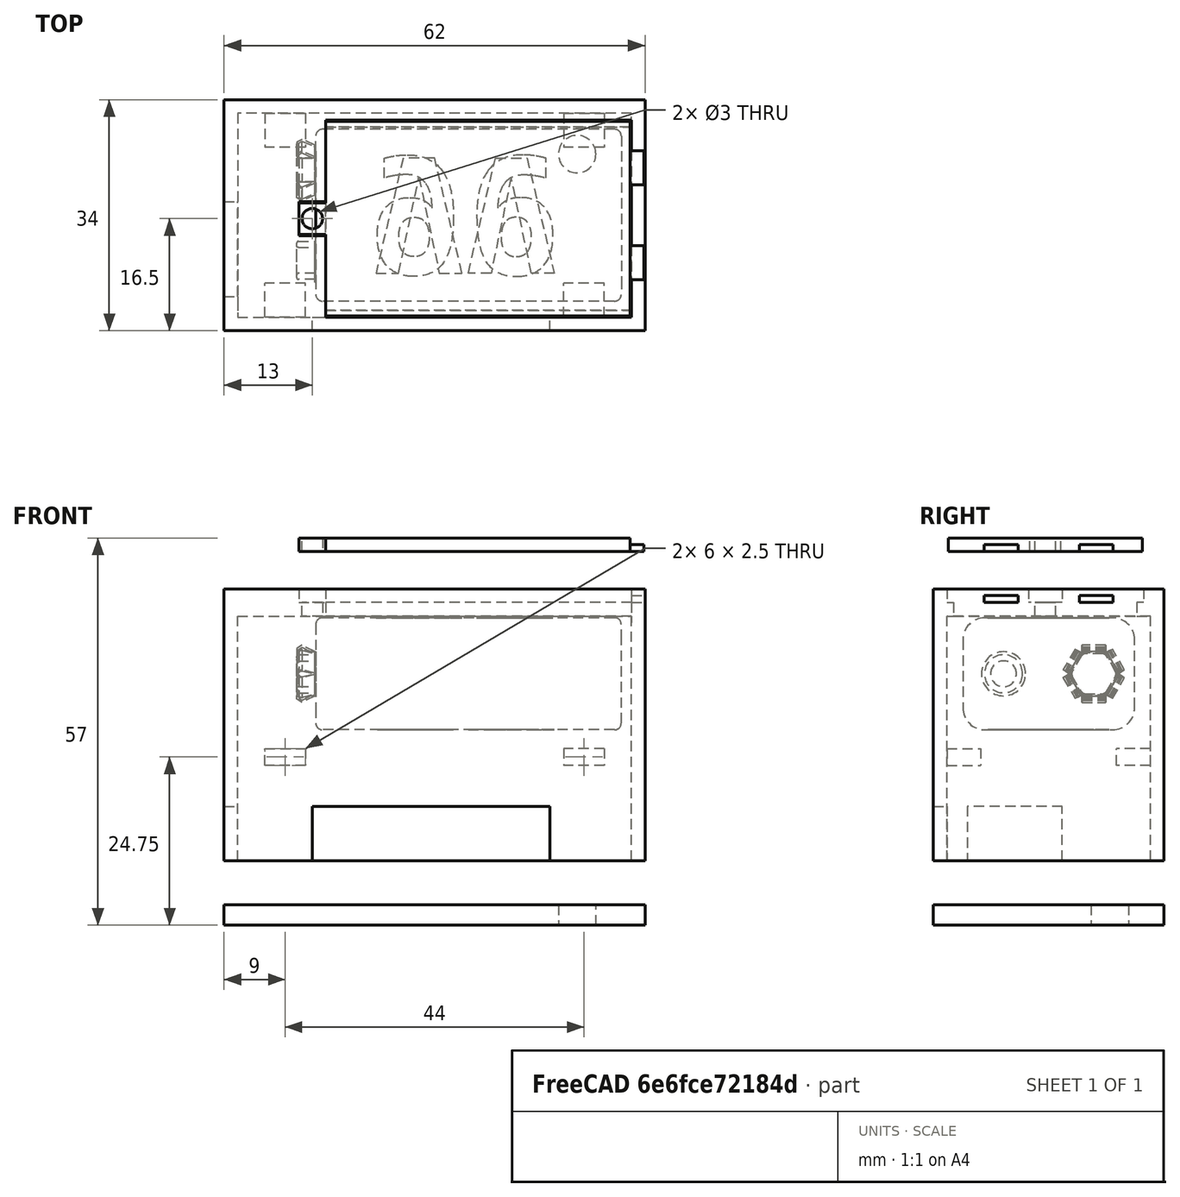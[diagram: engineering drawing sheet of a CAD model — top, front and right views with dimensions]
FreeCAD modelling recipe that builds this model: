
FCSTD DOCUMENT  (FreeCAD 0.20R29603 (Git))
Label: Remote Housing Revision 2
License: All rights reserved
LicenseURL: http://en.wikipedia.org/wiki/All_rights_reserved
objects: Sketcher::SketchObject×15, PartDesign::Pocket×9, PartDesign::Pad×6, Mesh::Feature×4, PartDesign::Body×3, Part::Feature×1
note: 49 computed .brp shape members not serialized (recipe doc carries the construction recipe); baked Part::Feature solids carry a one-line shape summary decoded from their .brp

FEATURE [Mesh::Feature] Unnamed_Goouuu_ESP32_Development_Board001  label="ESP32_Development_Board"
  Placement = pos=(-3.3e-15,12,-7) rot=(-0.57735,-0.57735,0.57735;2.0944rad)
FEATURE [Mesh::Feature] Switch
  Placement = pos=(-21,16,-13) rot=(0,0,1;1.5708rad)
FEATURE [Mesh::Feature] Switch001
  Placement = pos=(19,5,-19.5) rot=(-1,0,0;3.14159rad)
FEATURE [Mesh::Feature] Switch002
  Placement = pos=(-1.5,5,-19.5) rot=(1,0,0;3.14159rad)
FEATURE [Part::Feature] Solid  label="9V Battery"
  Placement = pos=(27.5,12,7) rot=(0.57735,-0.57735,-0.57735;2.0944rad)
  shape: bbox 47.8 x 25.84 x 17.04 mm, 172 faces (baked)
FEATURE [Sketcher::SketchObject] Sketch
  AttachmentOffset = pos=(0,0,16) rot=(0,0,1;0rad)
  FullyConstrained = true
  MapMode = 5
  Placement = pos=(0,0,16) rot=(0,0,1;0rad)
  Support = -> [XY_Plane]
  sketch-geometry (4):
    g0: LineSegment StartX=-31 StartY=29 StartZ=0 EndX=31 EndY=29 EndZ=0
    g1: LineSegment StartX=31 StartY=29 StartZ=0 EndX=31 EndY=-5 EndZ=0
    g2: LineSegment StartX=31 StartY=-5 StartZ=0 EndX=-31 EndY=-5 EndZ=0
    g3: LineSegment StartX=-31 StartY=-5 StartZ=0 EndX=-31 EndY=29 EndZ=0
  constraints (12):
    c: Horizontal(g0)
    c: Vertical(g1)
    c: Horizontal(g2)
    c: Vertical(g3)
    c: Coincident(g0,g3)
    c: Coincident(g2,g3)
    c: Coincident(g2,g1)
    c: Coincident(g1,g0)
    c: DistanceX(g-1,g1) = 31
    c: DistanceX(g2,g-1) = 31
    c: DistanceY(g-1,g0) = 29
    c: DistanceY(g1,g-1) = 5
FEATURE [PartDesign::Pad] Pad
  Direction = (0,0,1)
  Length = 40
  Length2 = 10
  Profile = -> Sketch
  ReferenceAxis = -> Sketch [N_Axis]
  Type = 0
FEATURE [Sketcher::SketchObject] Sketch001  label="Internal Cutout"
  FullyConstrained = true
  MapMode = 5
  Placement = pos=(0,0,16) rot=(1,0,0;3.14159rad)
  Support = -> [Pad]
  sketch-geometry (4):
    g0: LineSegment StartX=-29 StartY=-27 StartZ=0 EndX=-29 EndY=3 EndZ=0
    g1: LineSegment StartX=-29 StartY=3 StartZ=0 EndX=29 EndY=3 EndZ=0
    g2: LineSegment StartX=29 StartY=3 StartZ=0 EndX=29 EndY=-27 EndZ=0
    g3: LineSegment StartX=29 StartY=-27 StartZ=0 EndX=-29 EndY=-27 EndZ=0
  constraints (12):
    c: Vertical(g0)
    c: Horizontal(g1)
    c: Vertical(g2)
    c: Horizontal(g3)
    c: Coincident(g0,g1)
    c: Coincident(g0,g3)
    c: Coincident(g2,g3)
    c: Coincident(g1,g2)
    c: DistanceX(g-1,g1) = 29
    c: DistanceX(g0,g-1) = 29
    c: DistanceY(g2,g-1) = 27
    c: DistanceY(g-1,g1) = 3
FEATURE [PartDesign::Pocket] Pocket
  BaseFeature = -> Pad
  Direction = (0,0,1)
  Length = 36
  Length2 = 5
  Profile = -> Sketch001
  ReferenceAxis = -> Sketch001 [N_Axis]
  Type = 0
FEATURE [Sketcher::SketchObject] Sketch002  label="Battery Door Hole"
  FullyConstrained = true
  MapMode = 5
  Placement = pos=(0,0,56) rot=(0,0,1;0rad)
  Support = -> [Pocket]
  sketch-geometry (4):
    g0: LineSegment StartX=-16 StartY=25 StartZ=0 EndX=29 EndY=25 EndZ=0
    g1: LineSegment StartX=29 StartY=25 StartZ=0 EndX=29 EndY=-2 EndZ=0
    g2: LineSegment StartX=29 StartY=-2 StartZ=0 EndX=-16 EndY=-2 EndZ=0
    g3: LineSegment StartX=-16 StartY=-2 StartZ=0 EndX=-16 EndY=25 EndZ=0
  constraints (12):
    c: Horizontal(g0)
    c: Vertical(g1)
    c: Horizontal(g2)
    c: Vertical(g3)
    c: Coincident(g3,g0)
    c: Coincident(g1,g0)
    c: Coincident(g1,g2)
    c: Coincident(g2,g3)
    c: DistanceX(g-1,g1) = 29
    c: DistanceX(g2,g-1) = 16
    c: DistanceY(g-1,g0) = 25
    c: DistanceY(g2,g-1) = 2
FEATURE [PartDesign::Pocket] Pocket001
  BaseFeature = -> Pocket
  Direction = (0,0,-1)
  Length = 5
  Length2 = 5
  Profile = -> Sketch002
  ReferenceAxis = -> Sketch002 [N_Axis]
  Type = 0
FEATURE [Sketcher::SketchObject] Sketch003  label="Battery Door Hole 2"
  FullyConstrained = true
  MapMode = 5
  Placement = pos=(0,0,56) rot=(0,0,1;0rad)
  Support = -> [Pocket001]
  sketch-geometry (8):
    g0: LineSegment StartX=-16 StartY=26 StartZ=0 EndX=29 EndY=26 EndZ=0
    g1: LineSegment StartX=29 StartY=26 StartZ=0 EndX=29 EndY=-3 EndZ=0
    g2: LineSegment StartX=29 StartY=-3 StartZ=0 EndX=-16 EndY=-3 EndZ=0
    g3: LineSegment StartX=-16 StartY=-3 StartZ=0 EndX=-16 EndY=9 EndZ=0
    g4: LineSegment StartX=-20 StartY=9 StartZ=0 EndX=-16 EndY=9 EndZ=0
    g5: LineSegment StartX=-20 StartY=14 StartZ=0 EndX=-16 EndY=14 EndZ=0
    g6: LineSegment StartX=-16 StartY=14 StartZ=0 EndX=-16 EndY=26 EndZ=0
    g7: LineSegment StartX=-20 StartY=14 StartZ=0 EndX=-20 EndY=9 EndZ=0
  constraints (24):
    c: Horizontal(g0)
    c: Vertical(g1)
    c: Horizontal(g2)
    c: Vertical(g3)
    c: Vertical(g6)
    c: Coincident(g0,g6)
    c: Coincident(g6,g5)
    c: Coincident(g4,g3)
    c: Coincident(g3,g2)
    c: Coincident(g2,g1)
    c: Coincident(g0,g1)
    c: DistanceX(g-1,g1) = 29
    c: DistanceX(g2,g-1) = 16
    c: DistanceY(g-1,g0) = 26
    c: DistanceY(g2,g-1) = 3
    c: DistanceY(g-1,g3) = 9
    c: DistanceY(g4,g5) = 5
    c: Vertical(g7)
    c: Coincident(g7,g5)
    c: Coincident(g7,g4)
    c: DistanceX(g4,g-1) = 20
    c: DistanceX(g5,g-1) = 16
    c: DistanceY(g-1,g4) = 9
    c: DistanceY(g-1,g5) = 14
FEATURE [PartDesign::Pocket] Pocket002
  BaseFeature = -> Pocket001
  Direction = (0,0,-1)
  Length = 2
  Length2 = 5
  Profile = -> Sketch003
  ReferenceAxis = -> Sketch003 [N_Axis]
  Type = 0
FEATURE [Sketcher::SketchObject] Sketch004  label="Battery Door Screw Hole"
  FullyConstrained = true
  MapMode = 5
  Placement = pos=(0,0,54) rot=(0,0,1;0rad)
  Support = -> [Pocket002]
  sketch-geometry (1):
    g0: Circle CenterX=-18 CenterY=11.5 CenterZ=0 NormalX=0 NormalY=0 NormalZ=1 AngleXU=0 Radius=1.5
  constraints (3):
    c: Diameter(g0) = 3
    c: DistanceX(g0,g-1) = 18
    c: DistanceY(g-1,g0) = 11.5
FEATURE [PartDesign::Pocket] Pocket003
  BaseFeature = -> Pocket002
  Direction = (0,0,-1)
  Length = 5
  Length2 = 5
  Profile = -> Sketch004
  ReferenceAxis = -> Sketch004 [N_Axis]
  Type = 0
FEATURE [Sketcher::SketchObject] Sketch005  label="Battery Door Hinge"
  FullyConstrained = true
  MapMode = 5
  Placement = pos=(29,0,0) rot=(0.57735,-0.57735,-0.57735;2.0944rad)
  Support = -> [Pocket003]
  sketch-geometry (8):
    g0: LineSegment StartX=-21.5 StartY=55 StartZ=0 EndX=-16.5 EndY=55 EndZ=0
    g1: LineSegment StartX=-16.5 StartY=55 StartZ=0 EndX=-16.5 EndY=54 EndZ=0
    g2: LineSegment StartX=-21.5 StartY=54 StartZ=0 EndX=-16.5 EndY=54 EndZ=0
    g3: LineSegment StartX=-21.5 StartY=55 StartZ=0 EndX=-21.5 EndY=54 EndZ=0
    g4: LineSegment StartX=-7.5 StartY=55 StartZ=0 EndX=-2.5 EndY=55 EndZ=0
    g5: LineSegment StartX=-2.5 StartY=55 StartZ=0 EndX=-2.5 EndY=54 EndZ=0
    g6: LineSegment StartX=-2.5 StartY=54 StartZ=0 EndX=-7.5 EndY=54 EndZ=0
    g7: LineSegment StartX=-7.5 StartY=54 StartZ=0 EndX=-7.5 EndY=55 EndZ=0
  constraints (24):
    c: Horizontal(g0)
    c: Horizontal(g2)
    c: Horizontal(g4)
    c: Horizontal(g6)
    c: Coincident(g4,g7)
    c: Coincident(g7,g6)
    c: Coincident(g6,g5)
    c: Coincident(g5,g4)
    c: Coincident(g0,g1)
    c: Coincident(g1,g2)
    c: Coincident(g3,g2)
    c: Coincident(g0,g3)
    c: DistanceY(g-1,g4) = 55
    c: DistanceX(g4,g-1) = 2.5
    c: DistanceX(g4,g4) = 5
    c: DistanceY(g7,g7) = 1
    c: Angle(g7,g4) = 1.5708
    c: Angle(g5,g6) = 1.5708
    c: DistanceY(g-1,g0) = 55
    c: DistanceX(g0,g4) = 14
    c: DistanceX(g0,g0) = 5
    c: DistanceY(g1,g1) = 1
    c: Angle(g0,g1) = 1.5708
    c: Angle(g2,g3) = 1.5708
FEATURE [PartDesign::Pocket] Pocket004
  BaseFeature = -> Pocket003
  Direction = (1,0,0)
  Length = 5
  Length2 = 5
  Profile = -> Sketch005
  ReferenceAxis = -> Sketch005 [N_Axis]
  Type = 0
FEATURE [Sketcher::SketchObject] Sketch006  label="ESP32 Support 1"
  FullyConstrained = true
  MapMode = 5
  Placement = pos=(0,27,0) rot=(1,0,0;1.5708rad)
  Support = -> [Pocket004]
  sketch-geometry (8):
    g0: LineSegment StartX=-25 StartY=32.5 StartZ=0 EndX=-19 EndY=32.5 EndZ=0
    g1: LineSegment StartX=-19 StartY=32.5 StartZ=0 EndX=-19 EndY=30 EndZ=0
    g2: LineSegment StartX=-19 StartY=30 StartZ=0 EndX=-25 EndY=30 EndZ=0
    g3: LineSegment StartX=-25 StartY=32.5 StartZ=0 EndX=-25 EndY=30 EndZ=0
    g4: LineSegment StartX=19 StartY=32.5 StartZ=0 EndX=25 EndY=32.5 EndZ=0
    g5: LineSegment StartX=25 StartY=32.5 StartZ=0 EndX=25 EndY=30 EndZ=0
    g6: LineSegment StartX=25 StartY=30 StartZ=0 EndX=19 EndY=30 EndZ=0
    g7: LineSegment StartX=19 StartY=30 StartZ=0 EndX=19 EndY=32.5 EndZ=0
  constraints (24):
    c: Horizontal(g0)
    c: Vertical(g1)
    c: Horizontal(g2)
    c: Horizontal(g4)
    c: Horizontal(g6)
    c: Vertical(g7)
    c: Coincident(g7,g4)
    c: Coincident(g4,g5)
    c: Coincident(g5,g6)
    c: Coincident(g6,g7)
    c: Coincident(g0,g1)
    c: Coincident(g1,g2)
    c: Coincident(g2,g3)
    c: Coincident(g3,g0)
    c: DistanceY(g-1,g1) = 30
    c: DistanceY(g-1,g6) = 30
    c: DistanceY(g6,g4) = 2.5
    c: DistanceY(g1,g0) = 2.5
    c: DistanceX(g1,g-1) = 19
    c: DistanceX(g-1,g6) = 19
    c: DistanceX(g0,g0) = 6
    c: DistanceX(g4,g4) = 6
    c: Angle(g5,g6) = 1.5708
    c: Angle(g2,g3) = 1.5708
FEATURE [PartDesign::Pad] Pad001
  BaseFeature = -> Pocket004
  Direction = (0,-1,2e-16)
  Length = 5
  Length2 = 10
  Profile = -> Sketch006
  ReferenceAxis = -> Sketch006 [N_Axis]
  Type = 0
FEATURE [Sketcher::SketchObject] Sketch007  label="ESP32 Support 2"
  FullyConstrained = true
  MapMode = 5
  Placement = pos=(0,-3,0) rot=(0,0.707107,0.707107;3.14159rad)
  Support = -> [Pad001]
  sketch-geometry (8):
    g0: LineSegment StartX=-25 StartY=32.5 StartZ=0 EndX=-19 EndY=32.5 EndZ=0
    g1: LineSegment StartX=-25 StartY=30 StartZ=0 EndX=-19 EndY=30 EndZ=0
    g2: LineSegment StartX=-19 StartY=32.5 StartZ=0 EndX=-19 EndY=30 EndZ=0
    g3: LineSegment StartX=-25 StartY=32.5 StartZ=0 EndX=-25 EndY=30 EndZ=0
    g4: LineSegment StartX=19 StartY=30 StartZ=0 EndX=25 EndY=30 EndZ=0
    g5: LineSegment StartX=25 StartY=30 StartZ=0 EndX=25 EndY=32.5 EndZ=0
    g6: LineSegment StartX=25 StartY=32.5 StartZ=0 EndX=19 EndY=32.5 EndZ=0
    g7: LineSegment StartX=19 StartY=32.5 StartZ=0 EndX=19 EndY=30 EndZ=0
  constraints (24):
    c: Horizontal(g0)
    c: Horizontal(g4)
    c: Vertical(g7)
    c: Coincident(g6,g7)
    c: Coincident(g7,g4)
    c: Coincident(g4,g5)
    c: Coincident(g5,g6)
    c: Coincident(g2,g0)
    c: Coincident(g2,g1)
    c: Coincident(g1,g3)
    c: Coincident(g0,g3)
    c: DistanceY(g-1,g4) = 30
    c: DistanceY(g-1,g1) = 30
    c: DistanceY(g4,g6) = 2.5
    c: DistanceY(g2,g2) = 2.5
    c: DistanceX(g-1,g6) = 19
    c: DistanceX(g0,g-1) = 19
    c: DistanceX(g0,g0) = 6
    c: DistanceX(g6,g6) = 6
    c: Angle(g5,g4) = 1.5708
    c: Angle(g7,g6) = 1.5708
    c: Angle(g2,g1) = 1.5708
    c: Angle(g3,g0) = 1.5708
    c: DistanceY(g3,g3) = 2.5
FEATURE [PartDesign::Pad] Pad002
  BaseFeature = -> Pad001
  Direction = (0,1,-2e-16)
  Length = 5
  Length2 = 10
  Profile = -> Sketch007
  ReferenceAxis = -> Sketch007 [N_Axis]
  Type = 0
FEATURE [Sketcher::SketchObject] Sketch008  label="Top Switch Hole"
  FullyConstrained = true
  MapMode = 5
  Placement = pos=(-31,0,0) rot=(0.57735,-0.57735,-0.57735;2.0944rad)
  Support = -> [Pad002]
  sketch-geometry (4):
    g0: LineSegment StartX=-14 StartY=24 StartZ=0 EndX=0 EndY=24 EndZ=0
    g1: LineSegment StartX=0 StartY=24 StartZ=0 EndX=0 EndY=16 EndZ=0
    g2: LineSegment StartX=0 StartY=16 StartZ=0 EndX=-14 EndY=16 EndZ=0
    g3: LineSegment StartX=-14 StartY=16 StartZ=0 EndX=-14 EndY=24 EndZ=0
  constraints (12):
    c: Horizontal(g0)
    c: Vertical(g1)
    c: Horizontal(g2)
    c: Vertical(g3)
    c: Coincident(g0,g3)
    c: Coincident(g2,g3)
    c: Coincident(g1,g2)
    c: Coincident(g1,g0)
    c: DistanceY(g-1,g1) = 16
    c: DistanceX(g1,g-1) = 0
    c: DistanceX(g0,g0) = 14
    c: DistanceY(g1,g1) = 8
FEATURE [PartDesign::Pocket] Pocket005
  BaseFeature = -> Pad002
  Direction = (1,0,0)
  Length = 5
  Length2 = 5
  Profile = -> Sketch008
  ReferenceAxis = -> Sketch008 [N_Axis]
  Type = 0
FEATURE [Sketcher::SketchObject] Sketch009  label="Switch Holes 2"
  FullyConstrained = true
  MapMode = 5
  Placement = pos=(0,-5,0) rot=(1,0,0;1.5708rad)
  Support = -> [Pocket005]
  sketch-geometry (4):
    g0: LineSegment StartX=-18 StartY=16 StartZ=0 EndX=17 EndY=16 EndZ=0
    g1: LineSegment StartX=17 StartY=16 StartZ=0 EndX=17 EndY=24 EndZ=0
    g2: LineSegment StartX=17 StartY=24 StartZ=0 EndX=-18 EndY=24 EndZ=0
    g3: LineSegment StartX=-18 StartY=24 StartZ=0 EndX=-18 EndY=16 EndZ=0
  constraints (12):
    c: Horizontal(g0)
    c: Vertical(g1)
    c: Horizontal(g2)
    c: Vertical(g3)
    c: Coincident(g2,g3)
    c: Coincident(g2,g1)
    c: Coincident(g1,g0)
    c: Coincident(g3,g0)
    c: DistanceX(g-1,g0) = 17
    c: DistanceY(g-1,g0) = 16
    c: DistanceX(g0,g0) = 35
    c: DistanceY(g1,g1) = 8
FEATURE [PartDesign::Pocket] Pocket006
  BaseFeature = -> Pocket005
  Direction = (0,1,-2e-16)
  Length = 5
  Length2 = 5
  Profile = -> Sketch009
  ReferenceAxis = -> Sketch009 [N_Axis]
  Type = 0
FEATURE [PartDesign::Body] Body  label="Housing Bottom"
  Group = -> [Sketch,Pad,Sketch001,Pocket,Sketch002,Pocket001,Sketch003,Pocket002,Sketch004,Pocket003,Sketch005,Pocket004,Sketch006,Pad001,Sketch007,Pad002,Sketch008,Pocket005,Sketch009,Pocket006]
  Origin = -> Origin
  Placement = pos=(0,0,-36.5) rot=(0,0,1;0rad)
  Tip = -> Pocket006
FEATURE [Sketcher::SketchObject] Sketch010  label="Battery Cover001"
  AttachmentOffset = pos=(0,0,25) rot=(0,0,1;0rad)
  FullyConstrained = true
  MapMode = 5
  Placement = pos=(0,0,25) rot=(0,0,1;0rad)
  Support = -> [XY_Plane001]
  sketch-geometry (8):
    g0: LineSegment StartX=-16 StartY=25.8 StartZ=0 EndX=28.8 EndY=25.8 EndZ=0
    g1: LineSegment StartX=28.8 StartY=25.8 StartZ=0 EndX=28.8 EndY=-2.8 EndZ=0
    g2: LineSegment StartX=28.8 StartY=-2.8 StartZ=0 EndX=-16 EndY=-2.8 EndZ=0
    g3: LineSegment StartX=-16 StartY=-2.8 StartZ=0 EndX=-16 EndY=9.2 EndZ=0
    g4: LineSegment StartX=-16 StartY=9.2 StartZ=0 EndX=-20 EndY=9.2 EndZ=0
    g5: LineSegment StartX=-20 StartY=9.2 StartZ=0 EndX=-20 EndY=13.8 EndZ=0
    g6: LineSegment StartX=-20 StartY=13.8 StartZ=0 EndX=-16 EndY=13.8 EndZ=0
    g7: LineSegment StartX=-16 StartY=13.8 StartZ=0 EndX=-16 EndY=25.8 EndZ=0
  constraints (24):
    c: Horizontal(g0)
    c: Vertical(g1)
    c: Horizontal(g2)
    c: Vertical(g3)
    c: Horizontal(g4)
    c: Vertical(g5)
    c: Horizontal(g6)
    c: Vertical(g7)
    c: Coincident(g6,g7)
    c: Coincident(g6,g5)
    c: Coincident(g4,g5)
    c: Coincident(g3,g4)
    c: Coincident(g2,g3)
    c: Coincident(g2,g1)
    c: Coincident(g0,g1)
    c: Coincident(g0,g7)
    c: DistanceX(g2,g-1) = 16
    c: DistanceX(g4,g-1) = 20
    c: DistanceX(g6,g-1) = 16
    c: DistanceX(g-1,g1) = 28.8
    c: DistanceY(g-1,g0) = 25.8
    c: DistanceY(g5,g5) = 4.6
    c: DistanceY(g-1,g4) = 9.2
    c: DistanceY(g2,g-1) = 2.8
FEATURE [PartDesign::Pad] Pad003
  Direction = (0,0,1)
  Length = 2
  Length2 = 10
  Profile = -> Sketch010
  ReferenceAxis = -> Sketch010 [N_Axis]
  Type = 0
FEATURE [Sketcher::SketchObject] Sketch011  label="Battery Cover Screw Hole "
  FullyConstrained = true
  MapMode = 5
  Placement = pos=(0,0,27) rot=(0,0,1;0rad)
  Support = -> [Pad003]
  sketch-geometry (1):
    g0: Circle CenterX=-18 CenterY=11.5 CenterZ=0 NormalX=0 NormalY=0 NormalZ=1 AngleXU=0 Radius=1.5
  constraints (3):
    c: Diameter(g0) = 3
    c: DistanceX(g0,g-1) = 18
    c: DistanceY(g-1,g0) = 11.5
FEATURE [PartDesign::Pocket] Pocket007
  BaseFeature = -> Pad003
  Direction = (0,0,-1)
  Length = 5
  Length2 = 5
  Profile = -> Sketch011
  ReferenceAxis = -> Sketch011 [N_Axis]
  Type = 0
FEATURE [Sketcher::SketchObject] Sketch012  label="Battery Cover Hinge"
  FullyConstrained = true
  MapMode = 5
  Placement = pos=(28.8,0,0) rot=(0.57735,0.57735,0.57735;2.0944rad)
  Support = -> [Pocket007]
  sketch-geometry (8):
    g0: LineSegment StartX=2.5 StartY=26 StartZ=0 EndX=7.5 EndY=26 EndZ=0
    g1: LineSegment StartX=7.5 StartY=26 StartZ=0 EndX=7.5 EndY=25 EndZ=0
    g2: LineSegment StartX=7.5 StartY=25 StartZ=0 EndX=2.5 EndY=25 EndZ=0
    g3: LineSegment StartX=2.5 StartY=26 StartZ=0 EndX=2.5 EndY=25 EndZ=0
    g4: LineSegment StartX=16.5 StartY=26 StartZ=0 EndX=21.5 EndY=26 EndZ=0
    g5: LineSegment StartX=21.5 StartY=26 StartZ=0 EndX=21.5 EndY=25 EndZ=0
    g6: LineSegment StartX=21.5 StartY=25 StartZ=0 EndX=16.5 EndY=25 EndZ=0
    g7: LineSegment StartX=16.5 StartY=25 StartZ=0 EndX=16.5 EndY=26 EndZ=0
  constraints (24):
    c: Horizontal(g0)
    c: Vertical(g1)
    c: Horizontal(g2)
    c: Coincident(g3,g0)
    c: Coincident(g3,g2)
    c: Coincident(g1,g0)
    c: Coincident(g1,g2)
    c: DistanceY(g-1,g2) = 25
    c: DistanceX(g-1,g2) = 2.5
    c: DistanceX(g0,g0) = 5
    c: DistanceY(g1,g1) = 1
    c: Angle(g3,g0) = 1.5708
    c: Horizontal(g4)
    c: Vertical(g5)
    c: Horizontal(g6)
    c: Coincident(g7,g4)
    c: Coincident(g6,g7)
    c: Coincident(g6,g5)
    c: Coincident(g5,g4)
    c: DistanceX(g0,g4) = 14
    c: DistanceX(g4,g4) = 5
    c: DistanceY(g7,g7) = 1
    c: DistanceY(g-1,g6) = 25
    c: Angle(g7,g4) = 1.5708
FEATURE [PartDesign::Pad] Pad004
  BaseFeature = -> Pocket007
  Direction = (1,0,0)
  Length = 2
  Length2 = 10
  Profile = -> Sketch012
  ReferenceAxis = -> Sketch012 [N_Axis]
  Type = 0
FEATURE [PartDesign::Body] Body001  label="Battery Cover"
  Group = -> [Sketch010,Pad003,Sketch011,Pocket007,Sketch012,Pad004]
  Origin = -> Origin001
  Tip = -> Pad004
FEATURE [Sketcher::SketchObject] Sketch013  label="Top"
  AttachmentOffset = pos=(0,0,-30) rot=(0,0,1;0rad)
  FullyConstrained = true
  MapMode = 5
  Placement = pos=(0,0,-30) rot=(0,0,1;0rad)
  Support = -> [XY_Plane002]
  sketch-geometry (4):
    g0: LineSegment StartX=-31 StartY=29 StartZ=0 EndX=31 EndY=29 EndZ=0
    g1: LineSegment StartX=31 StartY=29 StartZ=0 EndX=31 EndY=-5 EndZ=0
    g2: LineSegment StartX=31 StartY=-5 StartZ=0 EndX=-31 EndY=-5 EndZ=0
    g3: LineSegment StartX=-31 StartY=-5 StartZ=0 EndX=-31 EndY=29 EndZ=0
  constraints (12):
    c: Horizontal(g0)
    c: Vertical(g1)
    c: Horizontal(g2)
    c: Vertical(g3)
    c: Coincident(g0,g3)
    c: Coincident(g2,g3)
    c: Coincident(g2,g1)
    c: Coincident(g1,g0)
    c: DistanceX(g-1,g1) = 31
    c: DistanceX(g2,g-1) = 31
    c: DistanceY(g-1,g0) = 29
    c: DistanceY(g1,g-1) = 5
FEATURE [PartDesign::Pad] Pad005
  Direction = (0,0,1)
  Length = 3
  Length2 = 10
  Profile = -> Sketch013
  ReferenceAxis = -> Sketch013 [N_Axis]
  Type = 0
FEATURE [Sketcher::SketchObject] Sketch014  label="LED Hole"
  FullyConstrained = true
  MapMode = 5
  Placement = pos=(0,0,-30) rot=(1,0,0;3.14159rad)
  Support = -> [Pad005]
  sketch-geometry (1):
    g0: Circle CenterX=21 CenterY=-21 CenterZ=0 NormalX=0 NormalY=0 NormalZ=1 AngleXU=0 Radius=2.75
  constraints (3):
    c: Diameter(g0) = 5.5
    c: DistanceX(g-1,g0) = 21
    c: DistanceY(g0,g-1) = 21
FEATURE [PartDesign::Pocket] Pocket008
  BaseFeature = -> Pad005
  Direction = (0,0,1)
  Length = 5
  Length2 = 5
  Profile = -> Sketch014
  ReferenceAxis = -> Sketch014 [N_Axis]
  Type = 0
FEATURE [PartDesign::Body] Body002  label="Housing Top"
  Group = -> [Sketch013,Pad005,Sketch014,Pocket008]
  Origin = -> Origin002
  Tip = -> Pocket008
